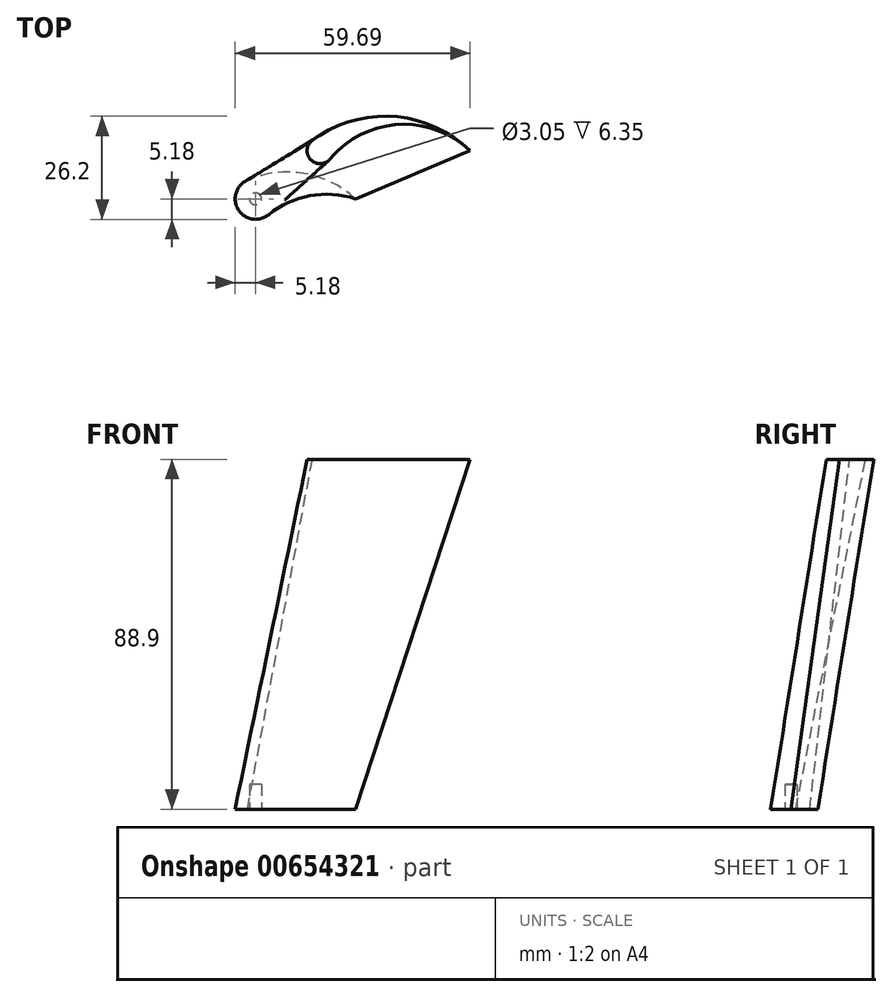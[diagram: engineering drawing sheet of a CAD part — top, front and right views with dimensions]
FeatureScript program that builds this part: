
annotation { "Feature Type Name" : "Feature", "Feature Type Description" : "" }
export const myFeature = defineFeature(function(context is Context, id is Id, definition is map)
    precondition{}
    {
        {
            var Q0;
            Q0=qCreatedBy(makeId("Top.planeOp"),FACE);
            var sketch = newSketch(context, id + "F0", { "sketchPlane" : qUnion([Q0])});
            skArc(sketch, "E0", {"start": v(-2.05, 4.76) * mm, "mid": v(-4.44, -2.68) * mm, "end": v(3.26, -4.03) * mm});
            skLineSegment(sketch, "E1", {"start": v(0, 0) * mm, "end": v(25.4, 0) * mm, "construction": true});
            skArc(sketch, "E2", {"start": v(25.4, 0) * mm, "mid": v(12.38, 6.47) * mm, "end": v(-2.05, 4.76) * mm});
            skArc(sketch, "E3", {"start": v(25.4, 0) * mm, "mid": v(13.81, 0.8) * mm, "end": v(3.26, -4.03) * mm});
            skSolve(sketch);
        }
        {
            var Q0;
            Q0=qCreatedBy(makeId("Top.planeOp"),FACE);
            cPlane(context, id + "F1", {"entities" : qUnion([Q0]), "cplaneType" : CPlaneType.OFFSET, "offset" : 88.9 * mm, "width" : 152.4 * mm, "height" : 152.4 * mm});
        }
        {
            var Q0;
            Q0=qCreatedBy(id+"F1.planeOp",FACE);
            var sketch = newSketch(context, id + "F2", { "sketchPlane" : qUnion([Q0])});
            skArc(sketch, "E4", {"start": v(14.44, 14.9) * mm, "mid": v(14.01, 9.97) * mm, "end": v(18.95, 10.14) * mm});
            skArc(sketch, "E5", {"start": v(54.5, 12.25) * mm, "mid": v(34.96, 20.95) * mm, "end": v(14.44, 14.9) * mm});
            skArc(sketch, "E6", {"start": v(54.5, 12.25) * mm, "mid": v(36.27, 18.91) * mm, "end": v(18.95, 10.14) * mm});
            skLineSegment(sketch, "E7", {"start": v(16.4, 12.25) * mm, "end": v(54.5, 12.25) * mm, "construction": true});
            skSolve(sketch);
        }
        {
            var Q0;
            Q0 = qSketchRegion(id + "F0", true);
            var Q1;
            Q1 = qSketchRegion(id + "F2", true);
            loft(context, id + "F3", {"sheetProfilesArray" : [{ "sheetProfileEntities" : qUnion([Q0]) }, { "sheetProfileEntities" : qUnion([Q1]) }]});
        }
        {
            var Q0;
            Q0=makeQuery(id+"F0.imprint","IMPRINT",FACE,{"disambiguationData":[TD([[makeQuery(id+"F0.imprint","IMPRINT",EDGE,{"derivedFrom":sQuery(id+"F0.wireOp",EDGE,"E0")}),1.0]])]});
            var sketch = newSketch(context, id + "F4", { "sketchPlane" : qUnion([Q0])});
            skCircle(sketch, "E8", {"center": v(0, 0) * mm, "radius": 1.52 * mm});
            skSolve(sketch);
        }
        {
            var Q0;
            Q0 = qSketchRegion(id + "F4", true);
            extrude(context, id + "F5", {"entities" : qUnion([Q0]), "operationType" : NewBodyOperationType.REMOVE, "oppositeDirection" : true, "depth" : -6.35 * mm, "offsetDistance" : 25.4 * mm});
        }
    });
